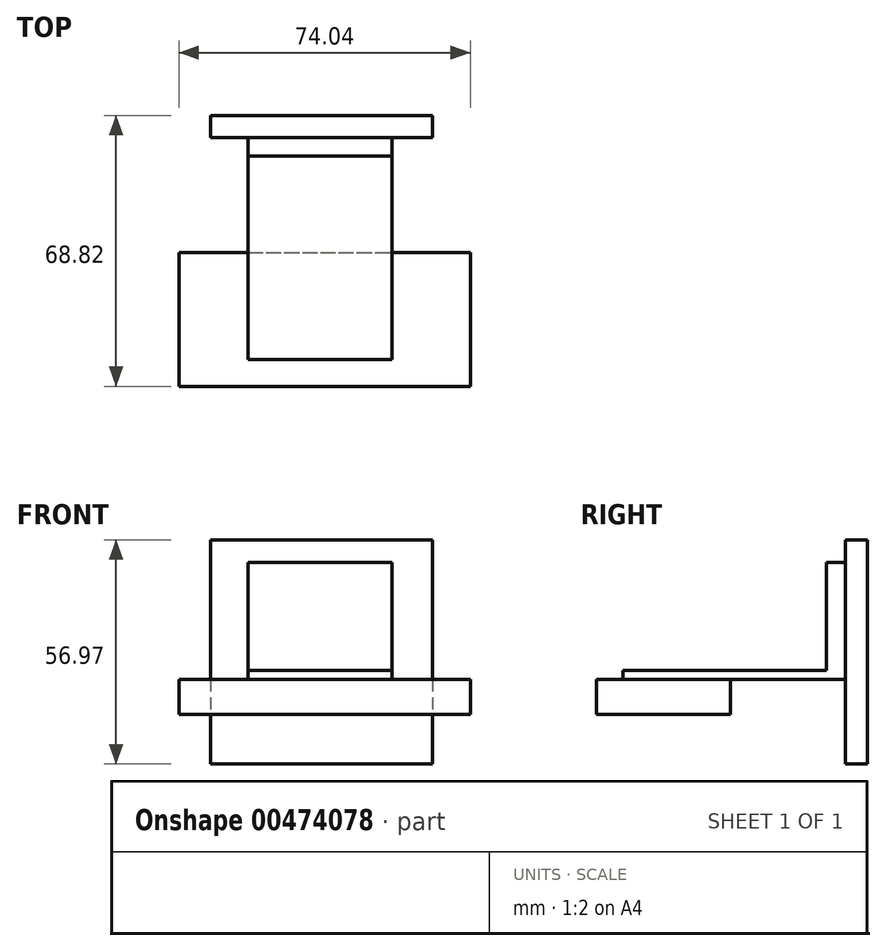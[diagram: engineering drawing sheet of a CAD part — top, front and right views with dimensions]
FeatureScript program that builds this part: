
annotation { "Feature Type Name" : "Feature", "Feature Type Description" : "" }
export const myFeature = defineFeature(function(context is Context, id is Id, definition is map)
    precondition{}
    {
        {
            var Q0;
            Q0=qCreatedBy(makeId("Front.planeOp"),FACE);
            var sketch = newSketch(context, id + "F0", { "sketchPlane" : qUnion([Q0])});
            skLineSegment(sketch, "E0.bottom", {"start": v(-22.1, 35.47) * mm, "end": v(34.26, 35.47) * mm});
            skLineSegment(sketch, "E0.top", {"start": v(-22.1, -21.5) * mm, "end": v(34.26, -21.5) * mm});
            skLineSegment(sketch, "E0.left", {"start": v(-22.1, 35.47) * mm, "end": v(-22.1, -21.5) * mm});
            skLineSegment(sketch, "E0.right", {"start": v(34.26, 35.47) * mm, "end": v(34.26, -21.5) * mm});
            skSolve(sketch);
        }
        {
            var Q0;
            Q0 = qSketchRegion(id + "F0", true);
            extrude(context, id + "F1", {"entities" : qUnion([Q0]), "depth" : 5.6 * mm});
        }
        {
            var Q0;
            Q0=qCreatedBy(makeId("Top.planeOp"),FACE);
            var sketch = newSketch(context, id + "F2", { "sketchPlane" : qUnion([Q0])});
            skLineSegment(sketch, "E1.bottom", {"start": v(-30.1, -68.82) * mm, "end": v(43.95, -68.82) * mm});
            skLineSegment(sketch, "E1.top", {"start": v(-30.1, -34.8) * mm, "end": v(43.95, -34.8) * mm});
            skLineSegment(sketch, "E1.left", {"start": v(-30.1, -68.82) * mm, "end": v(-30.1, -34.8) * mm});
            skLineSegment(sketch, "E1.right", {"start": v(43.95, -68.82) * mm, "end": v(43.95, -34.8) * mm});
            skSolve(sketch);
        }
        {
            var Q0;
            Q0 = qSketchRegion(id + "F2", true);
            extrude(context, id + "F3", {"entities" : qUnion([Q0]), "oppositeDirection" : true, "depth" : 8.9 * mm});
        }
        {
            var Q0;
            Q0=makeQuery(id+"F3.opExtrude","CAP_FACE",FACE,{"disambiguationData":[OSD([sQuery(id+"F2.wireOp",EDGE,"E1.bottom"),sQuery(id+"F2.wireOp",EDGE,"E1.top"),sQuery(id+"F2.wireOp",EDGE,"E1.left"),sQuery(id+"F2.wireOp",EDGE,"E1.right")])],"isStart":true});
            var sketch = newSketch(context, id + "F4", { "sketchPlane" : qUnion([Q0])});
            skLineSegment(sketch, "E2.bottom", {"start": v(-12.55, -62.01) * mm, "end": v(24.06, -62.01) * mm});
            skLineSegment(sketch, "E2.top", {"start": v(-12.55, -5.59) * mm, "end": v(24.06, -5.59) * mm});
            skLineSegment(sketch, "E2.left", {"start": v(-12.55, -62.01) * mm, "end": v(-12.55, -5.59) * mm});
            skLineSegment(sketch, "E2.right", {"start": v(24.06, -62.01) * mm, "end": v(24.06, -5.59) * mm});
            skSolve(sketch);
        }
        {
            var Q0;
            {var subQ0=sQuery(id+"F4.wireOp",EDGE,"E2.bottom");Q0=makeQuery(id+"F4.imprint","IMPRINT",FACE,{"disambiguationData":[TD([[makeQuery(id+"F4.imprint","IMPRINT",EDGE,{"derivedFrom":subQ0}),1.0]])]});}
            var Q1;
            {var subQ0=sQuery(id+"F4.wireOp",EDGE,"E2.top");Q1=makeQuery(id+"F4.imprint","IMPRINT",FACE,{"disambiguationData":[TD([[makeQuery(id+"F4.imprint","IMPRINT",EDGE,{"derivedFrom":subQ0}),-1.0]])]});}
            extrude(context, id + "F5", {"entities" : qUnion([Q0, Q1]), "depth" : 2.3 * mm});
        }
        {
            var Q0;
            Q0=makeQuery(id+"F5.opExtrude","CAP_FACE",FACE,{"disambiguationData":[OSD([sQuery(id+"F4.wireOp",EDGE,"E2.bottom"),sQuery(id+"F4.wireOp",EDGE,"E2.top"),sQuery(id+"F4.wireOp",EDGE,"E2.left"),sQuery(id+"F4.wireOp",EDGE,"E2.right")])],"isStart":false});
            var sketch = newSketch(context, id + "F6", { "sketchPlane" : qUnion([Q0])});
            skLineSegment(sketch, "E3.bottom", {"start": v(24.06, -5.59) * mm, "end": v(-12.55, -5.59) * mm});
            skLineSegment(sketch, "E3.top", {"start": v(24.06, -10.32) * mm, "end": v(-12.55, -10.32) * mm});
            skLineSegment(sketch, "E3.left", {"start": v(24.06, -5.59) * mm, "end": v(24.06, -10.32) * mm});
            skLineSegment(sketch, "E3.right", {"start": v(-12.55, -5.59) * mm, "end": v(-12.55, -10.32) * mm});
            skSolve(sketch);
        }
        {
            var Q0;
            Q0 = qSketchRegion(id + "F6", true);
            extrude(context, id + "F7", {"entities" : qUnion([Q0]), "operationType" : NewBodyOperationType.ADD, "depth" : 27.43 * mm});
        }
    });
